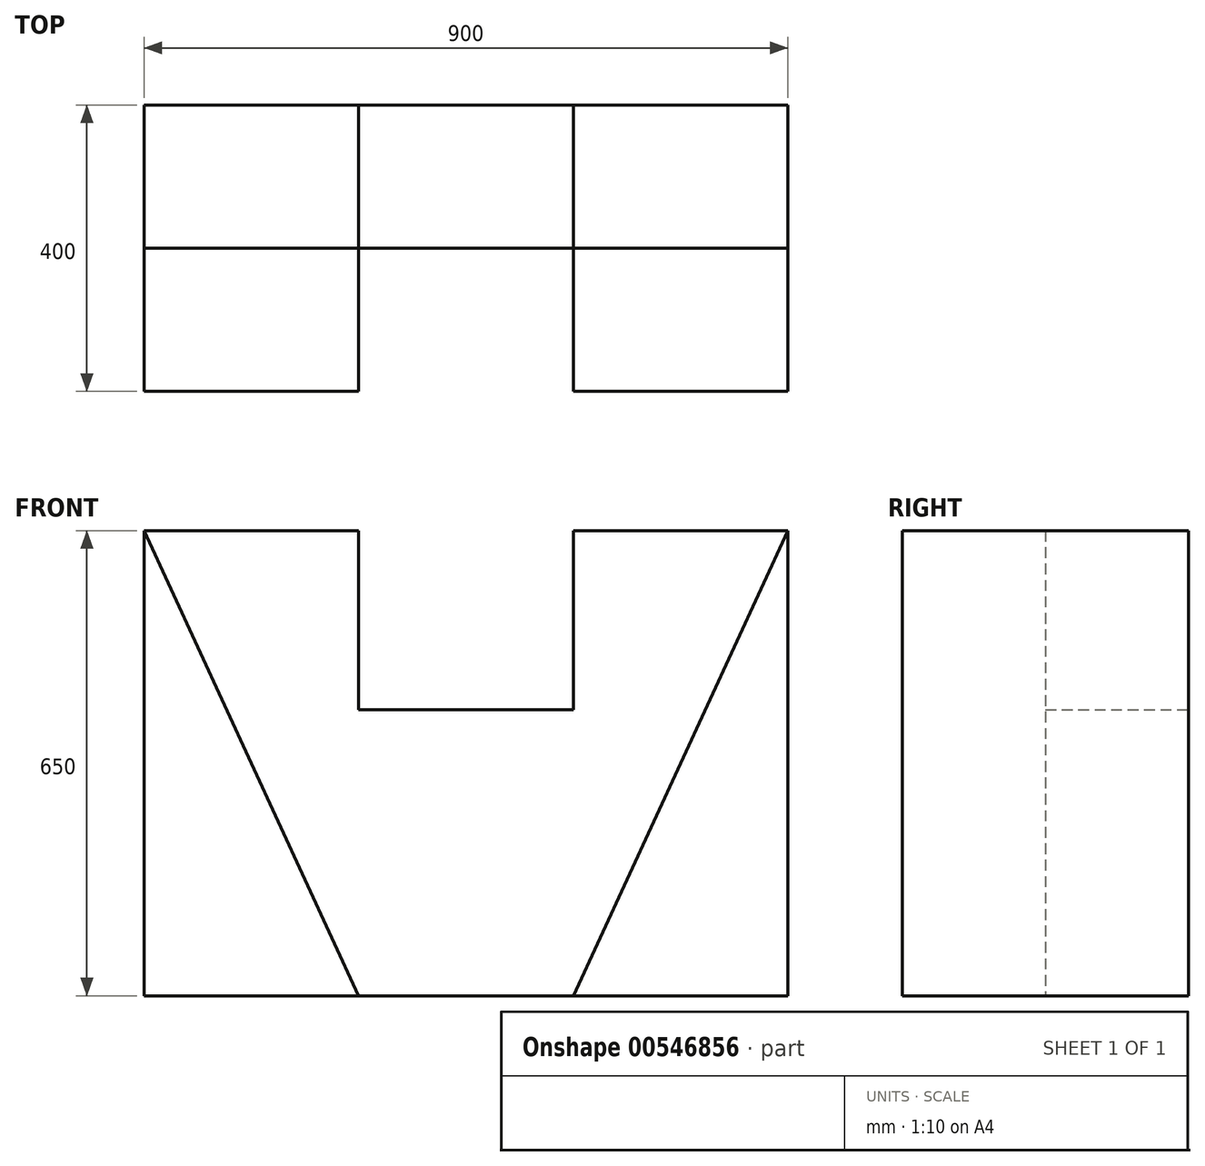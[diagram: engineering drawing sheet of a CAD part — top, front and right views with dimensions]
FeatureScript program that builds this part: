
annotation { "Feature Type Name" : "Feature", "Feature Type Description" : "" }
export const myFeature = defineFeature(function(context is Context, id is Id, definition is map)
    precondition{}
    {
        {
            var Q0;
            Q0=qCreatedBy(makeId("Front.planeOp"),FACE);
            var sketch = newSketch(context, id + "F0", { "sketchPlane" : qUnion([Q0])});
            skLineSegment(sketch, "E0.bottom", {"start": v(-450, -325) * mm, "end": v(450, -325) * mm});
            skLineSegment(sketch, "E0.top", {"start": v(-450, 325) * mm, "end": v(-150, 325) * mm});
            skLineSegment(sketch, "E0.left", {"start": v(-450, -325) * mm, "end": v(-450, 325) * mm});
            skLineSegment(sketch, "E0.right", {"start": v(450, -325) * mm, "end": v(450, 325) * mm});
            skPoint(sketch, "E0.middle", {"position": v(0, 0) * mm});
            skLineSegment(sketch, "E1", {"start": v(150, 325) * mm, "end": v(450, 325) * mm});
            skLineSegment(sketch, "E2", {"start": v(-150, 325) * mm, "end": v(-150, 75) * mm});
            skLineSegment(sketch, "E3", {"start": v(150, 325) * mm, "end": v(150, 75) * mm});
            skLineSegment(sketch, "E4", {"start": v(150, 75) * mm, "end": v(-150, 75) * mm});
            skSolve(sketch);
        }
        {
            var Q0;
            Q0 = qSketchRegion(id + "F0", true);
            extrude(context, id + "F1", {"entities" : qUnion([Q0]), "depth" : 200 * mm, "offsetDistance" : 25.4 * mm});
        }
        {
            var Q0;
            Q0=makeQuery(id+"F1.opExtrude","CAP_FACE",FACE,{"disambiguationData":[OSD([sQuery(id+"F0.wireOp",EDGE,"E0.bottom"),sQuery(id+"F0.wireOp",EDGE,"E0.left"),sQuery(id+"F0.wireOp",EDGE,"E0.right"),sQuery(id+"F0.wireOp",EDGE,"E0.top"),sQuery(id+"F0.wireOp",EDGE,"E2"),sQuery(id+"F0.wireOp",EDGE,"E3"),sQuery(id+"F0.wireOp",EDGE,"E4"),sQuery(id+"F0.wireOp",EDGE,"E1")])],"isStart":false});
            var sketch = newSketch(context, id + "F2", { "sketchPlane" : qUnion([Q0])});
            skLineSegment(sketch, "E5", {"start": v(-450, -325) * mm, "end": v(-450, 325) * mm});
            skLineSegment(sketch, "E6", {"start": v(-450, 325) * mm, "end": v(-150, -325) * mm});
            skLineSegment(sketch, "E7", {"start": v(-150, -325) * mm, "end": v(-450, -325) * mm});
            skLineSegment(sketch, "E8", {"start": v(-150, -325) * mm, "end": v(150, -325) * mm});
            skLineSegment(sketch, "E9", {"start": v(150, -325) * mm, "end": v(450, -325) * mm});
            skLineSegment(sketch, "E10", {"start": v(450, -325) * mm, "end": v(450, 325) * mm});
            skLineSegment(sketch, "E11", {"start": v(450, 325) * mm, "end": v(150, -325) * mm});
            skSolve(sketch);
        }
        {
            var Q0;
            Q0 = qSketchRegion(id + "F2", true);
            extrude(context, id + "F3", {"entities" : qUnion([Q0]), "operationType" : NewBodyOperationType.ADD, "depth" : 200 * mm, "offsetDistance" : 25.4 * mm});
        }
    });
